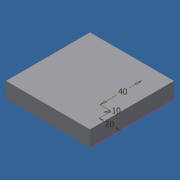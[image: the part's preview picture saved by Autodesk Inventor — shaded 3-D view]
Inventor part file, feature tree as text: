
AUTODESK INVENTOR PART (.ipt)
format: ipt  version: 2018 (Build 220112000, 112)  size: 141,312 bytes
history: native  units: mm
features: extrude x5, sketch x5, other x1
ambient origin geometry x8: Origin, YZ Plane, XZ Plane, XY Plane, X Axis, Y Axis, Z Axis, Center Point
bodies: Solid1 (feature_tree)
feature tree (11):
  other  "<userpath>\OneDrive\Objet3D\3DPrinter\Parameters.xlsx"
  extrude  "Extrusion1"  Depth=80.0mm
  extrude  "Extrusion2"  Depth=15.0mm
  extrude  "Extrusion3"  Depth=12.2mm
  extrude  "Extrusion4"  Depth=16.2mm
  extrude  "Extrusion5"  Depth=5.5mm TaperAngle=0.0deg
  sketch  "Sketch1"  dims[d0=80.0mm d1=80.0mm]
  sketch  "Sketch2"  dims[d2=15.0mm d3=0.0mm d7=40.0mm]
  sketch  "Sketch3"  dims[d8=20.0mm d9=12.2mm]
  sketch  "Sketch4"  dims[d10=10.0mm d11=0.0mm d12=16.2mm]
  sketch  "Sketch5"  dims[d13=4.0mm d14=0.0mm d15=5.5mm d16=0.0mm d17=12.0mm d18=4.0mm d19=0.0mm d20=30.0mm d21=15.0mm]
